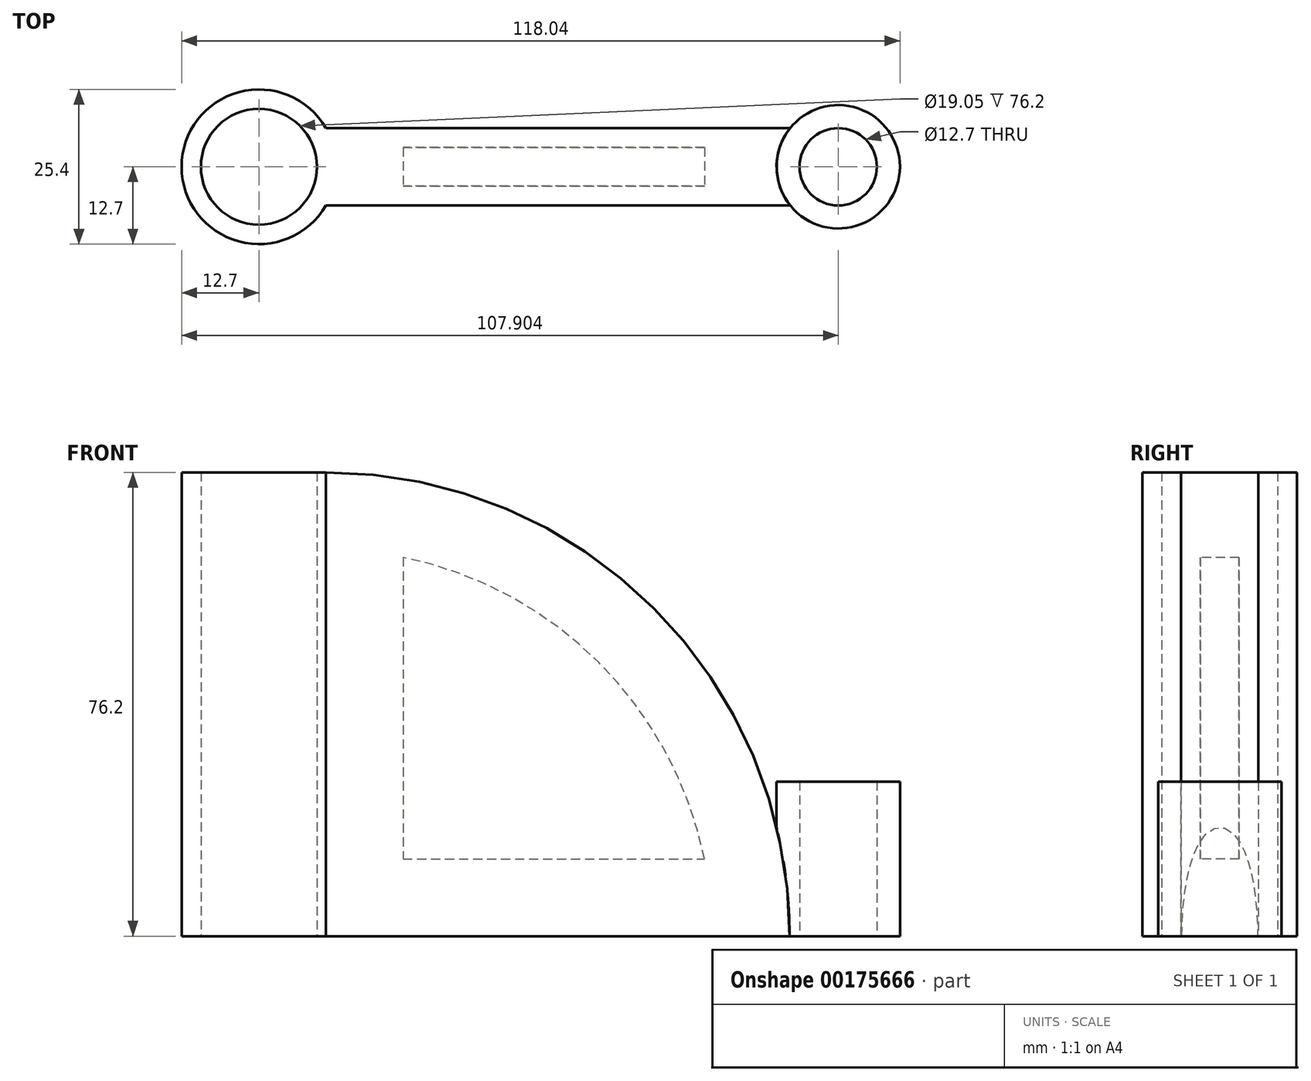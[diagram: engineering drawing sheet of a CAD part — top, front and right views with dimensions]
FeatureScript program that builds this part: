
annotation { "Feature Type Name" : "Feature", "Feature Type Description" : "" }
export const myFeature = defineFeature(function(context is Context, id is Id, definition is map)
    precondition{}
    {
        {
            var Q0;
            Q0=qCreatedBy(makeId("Top.planeOp"),FACE);
            var sketch = newSketch(context, id + "F0", { "sketchPlane" : qUnion([Q0])});
            skLineSegment(sketch, "E0", {"start": v(0, 0) * mm, "end": v(0, 52.02) * mm, "construction": true});
            skArc(sketch, "E1", {"start": v(11, 6.35) * mm, "mid": v(-12.7, 0) * mm, "end": v(11, -6.35) * mm});
            skCircle(sketch, "E2", {"center": v(0, 0) * mm, "radius": 9.53 * mm});
            skLineSegment(sketch, "E3.bottom", {"start": v(11, 6.35) * mm, "end": v(87.2, 6.35) * mm});
            skLineSegment(sketch, "E3.top", {"start": v(11, -6.35) * mm, "end": v(87.2, -6.35) * mm});
            skLineSegment(sketch, "E3.right", {"start": v(87.2, 6.35) * mm, "end": v(87.2, -6.35) * mm});
            skSolve(sketch);
        }
        {
            var Q0;
            Q0 = qSketchRegion(id + "F0", true);
            extrude(context, id + "F1", {"entities" : qUnion([Q0]), "depth" : 76.2 * mm});
        }
        {
            var Q0;
            Q0=makeQuery(id+"F1.opExtrude","SWEPT_FACE",FACE,{"disambiguationData":[OSD([sQuery(id+"F0.wireOp",EDGE,"E3.top")])]});
            var sketch = newSketch(context, id + "F2", { "sketchPlane" : qUnion([Q0])});
            skArc(sketch, "E4", {"start": v(87.2, 0) * mm, "mid": v(64.88, 53.88) * mm, "end": v(11, 76.2) * mm});
            skSolve(sketch);
        }
        {
            var Q0;
            Q0=makeQuery(id+"F2.imprint","IMPRINT",FACE,{"disambiguationData":[TD([[makeQuery(id+"F2.imprint","IMPRINT",EDGE,{"derivedFrom":sQuery(id+"F2.wireOp",EDGE,"E4")}),-1.0]])]});
            extrude(context, id + "F3", {"entities" : qUnion([Q0]), "operationType" : NewBodyOperationType.REMOVE, "endBound" : BoundingType.THROUGH_ALL, "oppositeDirection" : true, "depth" : 25.4 * mm});
        }
        {
            var Q0;
            Q0=qCreatedBy(makeId("Top.planeOp"),FACE);
            var sketch = newSketch(context, id + "F4", { "sketchPlane" : qUnion([Q0])});
            skCircle(sketch, "E5", {"center": v(95.2, 0) * mm, "radius": 10.13 * mm});
            skCircle(sketch, "E6", {"center": v(95.2, 0) * mm, "radius": 6.35 * mm});
            skSolve(sketch);
        }
        {
            var Q0;
            Q0 = qSketchRegion(id + "F4", true);
            extrude(context, id + "F5", {"entities" : qUnion([Q0]), "operationType" : NewBodyOperationType.ADD, "depth" : 25.4 * mm});
        }
        {
            var Q0;
            Q0=qCreatedBy(makeId("Front.planeOp"),FACE);
            var sketch = newSketch(context, id + "F6", { "sketchPlane" : qUnion([Q0])});
            skLineSegment(sketch, "E7.0", {"start": v(23.7, 12.7) * mm, "end": v(73.22, 12.7) * mm});
            skLineSegment(sketch, "E7.1", {"start": v(23.7, 62.22) * mm, "end": v(23.7, 12.7) * mm});
            skArc(sketch, "E7.2", {"start": v(73.22, 12.7) * mm, "mid": v(55.9, 44.9) * mm, "end": v(23.7, 62.22) * mm});
            skSolve(sketch);
        }
        {
            var Q0;
            Q0 = qSketchRegion(id + "F6", true);
            extrude(context, id + "F7", {"entities" : qUnion([Q0]), "operationType" : NewBodyOperationType.REMOVE, "endBound" : BoundingType.SYMMETRIC, "oppositeDirection" : true, "depth" : 6.35 * mm});
        }
    });
